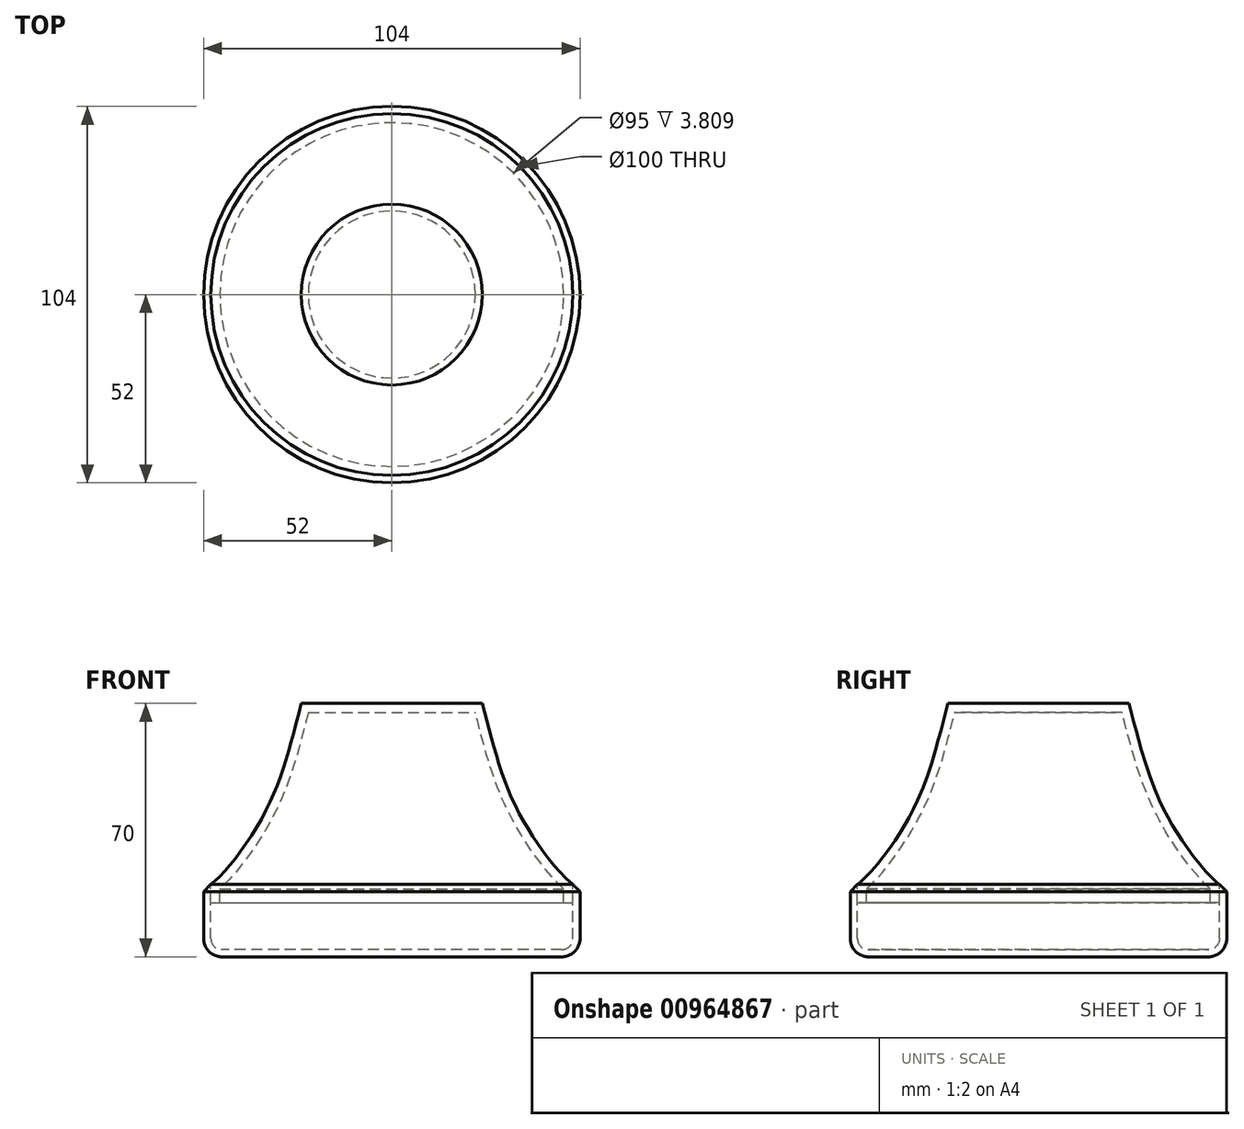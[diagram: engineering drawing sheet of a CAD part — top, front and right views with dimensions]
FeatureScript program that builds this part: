
annotation { "Feature Type Name" : "Feature", "Feature Type Description" : "" }
export const myFeature = defineFeature(function(context is Context, id is Id, definition is map)
    precondition{}
    {
        {
            var Q0;
            Q0=qCreatedBy(makeId("Front.planeOp"),FACE);
            var sketch = newSketch(context, id + "F0", { "sketchPlane" : qUnion([Q0])});
            skLineSegment(sketch, "E0", {"start": v(0, 50) * mm, "end": v(25, 50) * mm});
            skFitSpline(sketch, "E1", {"points": [v(25, 50) * mm, v(35, 20) * mm, v(50, 0) * mm], "startDerivative": vector(17.15, -64.6) * mm, "endDerivative": vector(25.5, -19.12) * mm});
            skLineSegment(sketch, "E2", {"start": v(50, 0) * mm, "end": v(0, 0) * mm});
            skLineSegment(sketch, "E3", {"start": v(0, 0) * mm, "end": v(0, 50) * mm});
            skSolve(sketch);
        }
        {
            var Q0;
            Q0=makeQuery(id+"F0.imprint","IMPRINT",FACE,{"disambiguationData":[TD([[makeQuery(id+"F0.imprint","IMPRINT",EDGE,{"derivedFrom":sQuery(id+"F0.wireOp",EDGE,"E0")}),-1.0]])]});
            var Q1;
            Q1=sQuery(id+"F0.wireOp",EDGE,"E3");
            revolve(context, id + "F1", {"surfaceOperationType" : NewSurfaceOperationType.NEW, "entities" : qUnion([Q0]), "axis" : qUnion([Q1]), "revolveType" : RevolveType.FULL});
        }
        {
            var Q0;
            Q0=makeQuery(id+"F1.opRevolve","SWEPT_FACE",FACE,{"disambiguationData":[OSD([sQuery(id+"F0.wireOp",EDGE,"E2")])]});
            var sketch = newSketch(context, id + "F2", { "sketchPlane" : qUnion([Q0])});
            skCircle(sketch, "E4.0.0", {"center": v(0, 0) * mm, "radius": 50 * mm});
            skSolve(sketch);
        }
        {
            var Q0;
            Q0=makeQuery(id+"F2.imprint","IMPRINT",FACE,{"disambiguationData":[TD([[makeQuery(id+"F2.imprint","IMPRINT",EDGE,{"derivedFrom":sQuery(id+"F2.wireOp",EDGE,"E4.0.0")}),1.0]])]});
            extrude(context, id + "F3", {"entities" : qUnion([Q0]), "operationType" : NewBodyOperationType.ADD, "depth" : 5 * mm, "offsetDistance" : 25 * mm});
        }
        {
            var Q0;
            Q0=makeQuery(id+"F3.opExtrude","CAP_FACE",FACE,{"disambiguationData":[OSD([sQuery(id+"F2.wireOp",EDGE,"E4.0.0")])],"isStart":false});
            shell(context, id + "F4", {"entities" : qUnion([Q0]), "thickness" : 2.5 * mm});
        }
        {
            var Q0;
            Q0=qCreatedBy(makeId("Top.planeOp"),FACE);
            var sketch = newSketch(context, id + "F5", { "sketchPlane" : qUnion([Q0])});
            skCircle(sketch, "E5.0", {"center": v(0, 0) * mm, "radius": 50 * mm, "construction": true});
            skCircle(sketch, "E6.0", {"center": v(0, 0) * mm, "radius": 52 * mm});
            skSolve(sketch);
        }
        {
            var Q0;
            Q0=makeQuery(id+"F5.imprint","IMPRINT",FACE,{"disambiguationData":[TD([[makeQuery(id+"F5.imprint","IMPRINT",EDGE,{"derivedFrom":sQuery(id+"F5.wireOp",EDGE,"E6.0")}),1.0]])]});
            var Q1;
            Q1=sQuery(id+"F5.wireOp",EDGE,"E5.0");
            extrude(context, id + "F6", {"entities" : qUnion([Q0]), "surfaceEntities" : qUnion([Q1]), "oppositeDirection" : true, "depth" : 20 * mm, "offsetDistance" : 25 * mm});
        }
        {
            var Q0;
            Q0=makeQuery(id+"F6.opExtrude","CAP_EDGE",EDGE,{"disambiguationData":[OSD([sQuery(id+"F5.wireOp",EDGE,"E6.0")])],"isStart":false});
            fillet(context, id + "F7", {"entities" : qUnion([Q0]), "radius" : 5 * mm, "tangentPropagation" : true, "allowEdgeOverflow" : false});
        }
        {
            var Q0;
            Q0=makeQuery(id+"F6.opExtrude","CAP_FACE",FACE,{"disambiguationData":[OSD([sQuery(id+"F5.wireOp",EDGE,"E6.0")])],"isStart":true});
            shell(context, id + "F8", {"entities" : qUnion([Q0]), "thickness" : 2 * mm});
        }
        {
            var Q0;
            Q0=makeQuery(id+"F6.opExtrude","CAP_EDGE",EDGE,{"disambiguationData":[OSD([sQuery(id+"F5.wireOp",EDGE,"E6.0")])],"isStart":true});
            chamfer(context, id + "F9", {"entities" : qUnion([Q0]), "width" : 2 * mm, "tangentPropagation" : true});
        }
    });
